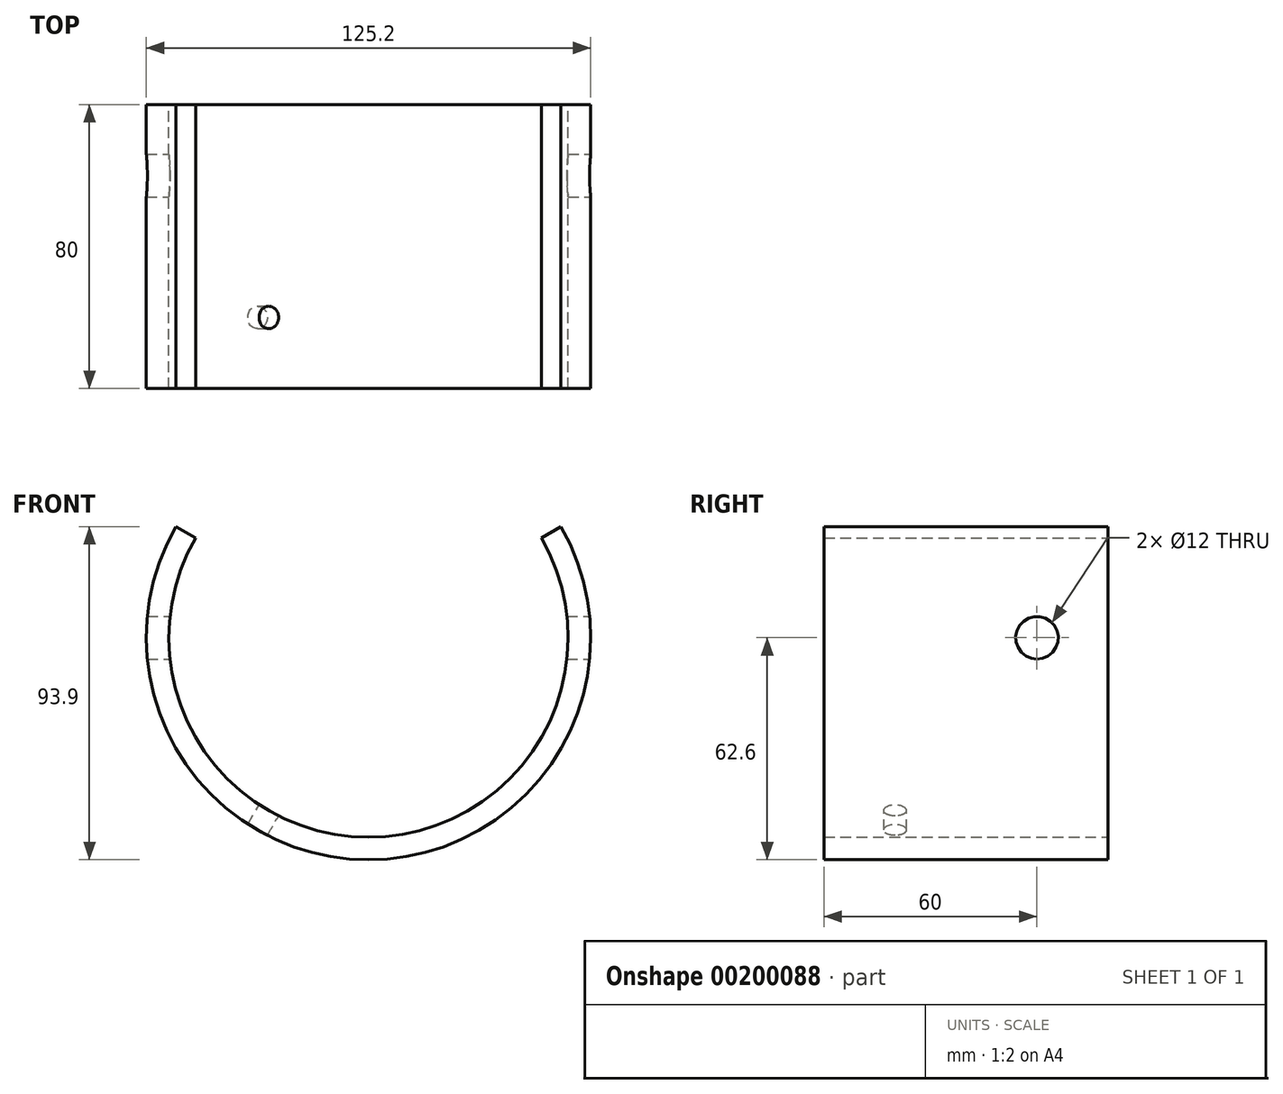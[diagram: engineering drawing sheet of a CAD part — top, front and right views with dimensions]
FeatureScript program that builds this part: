
annotation { "Feature Type Name" : "Feature", "Feature Type Description" : "" }
export const myFeature = defineFeature(function(context is Context, id is Id, definition is map)
    precondition{}
    {
        {
            var Q0;
            Q0=qCreatedBy(makeId("Front.planeOp"),FACE);
            var sketch = newSketch(context, id + "F0", { "sketchPlane" : qUnion([Q0])});
            skCircle(sketch, "E0", {"center": v(0, 0) * mm, "radius": 56.25 * mm});
            skCircle(sketch, "E1", {"center": v(0, 0) * mm, "radius": 62.6 * mm});
            skSolve(sketch);
        }
        {
            var Q0;
            Q0=makeQuery(id+"F0.imprint","IMPRINT",FACE,{"disambiguationData":[TD([[makeQuery(id+"F0.imprint","IMPRINT",EDGE,{"derivedFrom":sQuery(id+"F0.wireOp",EDGE,"E0")}),-1.0]])]});
            extrude(context, id + "F1", {"entities" : qUnion([Q0]), "endBound" : BoundingType.SYMMETRIC, "depth" : 80 * mm});
        }
        {
            var Q0;
            Q0=qCreatedBy(makeId("Right.planeOp"),FACE);
            var sketch = newSketch(context, id + "F2", { "sketchPlane" : qUnion([Q0])});
            skCircle(sketch, "E2", {"center": v(20, 0) * mm, "radius": 6 * mm});
            skSolve(sketch);
        }
        {
            var Q0;
            Q0 = qSketchRegion(id + "F2", true);
            extrude(context, id + "F3", {"entities" : qUnion([Q0]), "operationType" : NewBodyOperationType.REMOVE, "endBound" : BoundingType.SYMMETRIC, "oppositeDirection" : true, "depth" : 254 * mm});
        }
        {
            var Q0;
            Q0=makeQuery(id+"F1.opExtrude","CAP_FACE",FACE,{"disambiguationData":[OSD([sQuery(id+"F0.wireOp",EDGE,"E0"),sQuery(id+"F0.wireOp",EDGE,"E1")])],"isStart":false});
            var sketch = newSketch(context, id + "F4", { "sketchPlane" : qUnion([Q0])});
            skLineSegment(sketch, "E3", {"start": v(0, 0) * mm, "end": v(-170.57, 98.48) * mm});
            skLineSegment(sketch, "E4", {"start": v(-170.57, 98.48) * mm, "end": v(170.57, 98.48) * mm});
            skLineSegment(sketch, "E5", {"start": v(170.57, 98.48) * mm, "end": v(0, 0) * mm});
            skSolve(sketch);
        }
        {
            var Q0;
            {var subQ0=sQuery(id+"F4.wireOp",EDGE,"E5");var subQ1=sQuery(id+"F4.wireOp",EDGE,"E3");var subQ2=makeQuery(id+"F4.imprint","INTERSECT",VERTEX,{"derivedFrom":[subQ1,subQ0]});Q0=makeQuery(id+"F4.imprint","IMPRINT",FACE,{"disambiguationData":[TD([[makeQuery(id+"F4.imprint","IMPRINT",EDGE,{"disambiguationData":[TD([[subQ2,-1.0]])],"derivedFrom":subQ1}),-1.0]])]});}
            var Q1;
            {var subQ0=sQuery(id+"F4.wireOp",EDGE,"E3");var subQ1=makeQuery(id+"F1.opExtrude","CAP_EDGE",EDGE,{"disambiguationData":[OSD([sQuery(id+"F0.wireOp",EDGE,"E1")])],"isStart":false});var subQ2=makeQuery(id+"F4.imprint","INTERSECT",VERTEX,{"derivedFrom":[subQ1,subQ0]});Q1=makeQuery(id+"F4.imprint","IMPRINT",FACE,{"disambiguationData":[TD([[makeQuery(id+"F4.imprint","IMPRINT",EDGE,{"disambiguationData":[TD([[subQ2,1.0]])],"derivedFrom":subQ0}),-1.0]])]});}
            extrude(context, id + "F5", {"entities" : qUnion([Q0, Q1]), "operationType" : NewBodyOperationType.REMOVE, "endBound" : BoundingType.THROUGH_ALL, "oppositeDirection" : true, "depth" : 25.4 * mm});
        }
        {
            var Q0;
            Q0=makeQuery(id+"F1.opExtrude","CAP_FACE",FACE,{"disambiguationData":[OSD([sQuery(id+"F0.wireOp",EDGE,"E0"),sQuery(id+"F0.wireOp",EDGE,"E1")])],"isStart":false});
            var sketch = newSketch(context, id + "F6", { "sketchPlane" : qUnion([Q0])});
            skLineSegment(sketch, "E6", {"start": v(0, 0) * mm, "end": v(40.63, -23.46) * mm});
            skSolve(sketch);
        }
        {
            var Q0;
            Q0=qCreatedBy(makeId("Origin.pointOp"),VERTEX);
            var Q1;
            Q1=sQuery(id+"F6.wireOp",VERTEX,"E6.start");
            var Q2;
            Q2=sQuery(id+"F6.wireOp",VERTEX,"E6.end");
            cPlane(context, id + "F7", {"entities" : qUnion([Q0, Q1, Q2]), "cplaneType" : CPlaneType.THREE_POINT, "offset" : 25.4 * mm, "width" : 152.4 * mm, "height" : 152.4 * mm});
        }
        {
            var Q0;
            Q0=qCreatedBy(id+"F7.planeOp",FACE);
            var sketch = newSketch(context, id + "F8", { "sketchPlane" : qUnion([Q0])});
            skCircle(sketch, "E7", {"center": v(0, 20) * mm, "radius": 3.18 * mm});
            skSolve(sketch);
        }
        {
            var Q0;
            Q0=makeQuery(id+"F8.imprint","IMPRINT",FACE,{"disambiguationData":[TD([[makeQuery(id+"F8.imprint","IMPRINT",EDGE,{"derivedFrom":sQuery(id+"F8.wireOp",EDGE,"E7")}),1.0]])]});
            extrude(context, id + "F9", {"entities" : qUnion([Q0]), "operationType" : NewBodyOperationType.REMOVE, "depth" : 254 * mm});
        }
        {
            var Q0;
            Q0=qCreatedBy(makeId("Right.planeOp"),FACE);
            var sketch = newSketch(context, id + "F10", { "sketchPlane" : qUnion([Q0])});
            skLineSegment(sketch, "E8", {"start": v(0, 0) * mm, "end": v(-110.2, 0) * mm});
            skSolve(sketch);
        }
        {
            var Q0;
            Q0=qCreatedBy(makeId("Right.planeOp"),FACE);
            var sketch = newSketch(context, id + "F11", { "sketchPlane" : qUnion([Q0])});
            skLineSegment(sketch, "E9", {"start": v(0, 0) * mm, "end": v(141.67, 0) * mm});
            skSolve(sketch);
        }
    });
